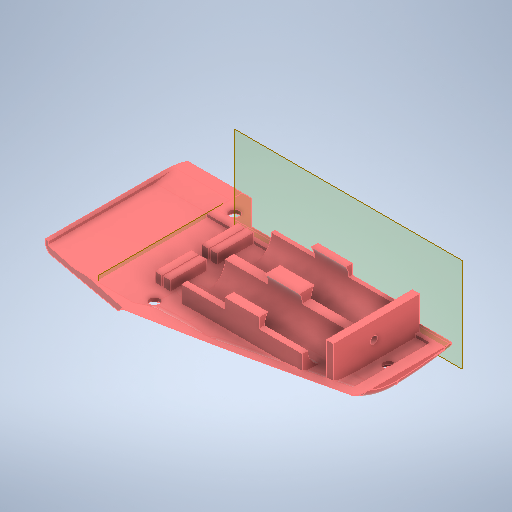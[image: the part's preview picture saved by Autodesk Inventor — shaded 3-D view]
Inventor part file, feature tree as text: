
AUTODESK INVENTOR PART (.ipt)
format: ipt  version: 2025 (Build 290162000, 162)  size: 3,606,528 bytes
history: native  units: in
note: dims shown in document units (in); Inventor stores cm internally (conversion verified against a paired STEP export)
features: extrude x48, sketch x39, fillet x33, other x28, reference x25, chamfer x10, projected_geometry x9, mirror x3, hole x1
ambient origin geometry x8: Origin, YZ Plane, XZ Plane, XY Plane, X Axis, Y Axis, Z Axis, Center Point
bodies: Body1 (feature_tree)
feature tree (196):
  other  "ソリッド1"
  sketch  "スケッチ1"
  extrude  "押し出し1"  Depth=3.3465in
  sketch  "スケッチ4"
  extrude  "押し出し4"  Depth=0.2756in
  extrude  "押し出し5"  Depth=9.8425in
  extrude  "押し出し6"  Depth=0.8661in TaperAngle=0.0deg
  extrude  "押し出し7"  Depth=0.8268in
  chamfer  "面取り1"  Distance=0.1181in
  chamfer  "面取り2"  Distance=0.1181in
  chamfer  "面取り3"  Distance=1.8504in
  chamfer  "面取り4"  Distance=1.1024in
  other  "作業平面3"
  other  "作業平面5"
  extrude  "押し出し8"  Depth=1.5354in
  other  "作業平面6"
  mirror  "ミラー1"
  chamfer  "面取り5"  Distance=3.3465in
  extrude  "押し出し9"  Depth=3.3465in TaperAngle=0.0deg
  fillet  "フィレット27"  Radius=3.3465in
  fillet  "フィレット28"  Radius=3.3465in
  fillet  "フィレット29"  Radius=0.1181in
  fillet  "フィレット30"  Radius=0.1181in
  fillet  "フィレット32"  Radius=0.1181in
  fillet  "フィレット35"  Radius=0.1181in
  fillet  "フィレット36"  Radius=0.3937in
  fillet  "フィレット37"  Radius=0.1575in
  fillet  "フィレット38"  Radius=0.7087in
  fillet  "フィレット42"  [1 undecoded]
  fillet  "フィレット43"  Radius=0.3543in
  fillet  "フィレット44"  Radius=1.9685in
  fillet  "フィレット45"  Radius=2.0866in
  other  "作業平面7"
  extrude  "押し出し10"  Depth=0.1969in
  fillet  "フィレット46"  Radius=0.1969in
  other  "作業平面8"
  extrude  "押し出し11"  Depth=0.7874in
  sketch  "スケッチ10"
  extrude  "押し出し12"  Depth=0.0787in
  extrude  "押し出し13"  Depth=0.3937in
  chamfer  "面取り6"  Distance=0.1181in
  sketch  "スケッチ11"
  chamfer  "面取り7"  Distance=0.1181in
  extrude  "押し出し14"  Depth=0.0354in
  chamfer  "面取り8"  Distance=0.0394in
  chamfer  "面取り9"  Distance=0.0787in
  extrude  "押し出し15"  Depth=0.0118in
  chamfer  "面取り10"  Distance=0.0354in
  other  "作業平面9"
  other  "作業平面10"
  extrude  "押し出し16"  [1 undecoded]
  fillet  "フィレット47"  Radius=0.0394in
  fillet  "フィレット48"  Radius=0.0394in
  fillet  "フィレット49"  Radius=0.0394in
  mirror  "ミラー7"
  mirror  "ミラー8"
  fillet  "フィレット58"  Radius=0.8268in
  fillet  "フィレット59"  Radius=0.0787in
  fillet  "フィレット60"  Radius=0.8268in
  fillet  "フィレット61"  Radius=1.1681in
  fillet  "フィレット62"  Radius=1.1681in
  fillet  "フィレット63"  Radius=0.6299in
  other  "作業平面11"
  extrude  "押し出し17"  TaperAngle=45.0deg  [1 undecoded]
  extrude  "押し出し18"  Depth=0.3937in
  extrude  "押し出し19"  Depth=1.1811in TaperAngle=0.0deg
  extrude  "押し出し20"  Depth=0.3543in TaperAngle=45.0deg
  other  "作業平面13"
  extrude  "押し出し21"  Depth=0.0787in
  fillet  "フィレット66"  Radius=0.1181in
  fillet  "フィレット67"  Radius=0.0709in
  extrude  "押し出し22"  Depth=0.0394in TaperAngle=45.0deg
  other  "作業平面14"
  extrude  "押し出し23"  Depth=0.0394in TaperAngle=45.0deg
  other  "作業平面15"
  extrude  "押し出し24"  Depth=0.0591in TaperAngle=0.0deg
  extrude  "押し出し25"  Depth=0.1969in TaperAngle=45.0deg
  other  "作業平面16"
  extrude  "押し出し26"  Depth=0.0591in TaperAngle=0.0deg
  extrude  "押し出し27"  Depth=3.937in
  other  "作業平面17"
  extrude  "押し出し28"  Depth=1.9685in
  extrude  "押し出し29"  Depth=0.1181in
  sketch  "スケッチ29"
  extrude  "押し出し30"  Depth=0.1181in
  extrude  "押し出し31"  Depth=0.0787in
  extrude  "押し出し32"  Depth=0.0197in
  extrude  "押し出し33"  Depth=0.0197in
  other  "作業平面18"
  extrude  "押し出し34"  Depth=0.3937in
  extrude  "押し出し35"  Depth=0.1181in
  fillet  "フィレット68"  [1 undecoded]
  fillet  "フィレット69"  Radius=1.1811in
  fillet  "フィレット70"  Radius=0.0787in
  fillet  "フィレット71"  Radius=0.1181in
  fillet  "フィレット72"  Radius=0.0197in
  extrude  "押し出し36"  Depth=0.0787in TaperAngle=0.0deg
  other  "作業平面19"
  fillet  "フィレット74"  Radius=0.9949in
  fillet  "フィレット75"  Radius=0.3937in
  fillet  "フィレット76"  Radius=0.0472in
  sketch  "スケッチ33"
  extrude  "押し出し39"  Depth=0.0669in
  extrude  "押し出し40"  Depth=0.0079in
  sketch  "スケッチ35"
  extrude  "押し出し41"  Depth=0.2756in
  other  "作業平面20"
  extrude  "押し出し42"  Depth=0.3543in
  sketch  "スケッチ37"
  extrude  "押し出し43"  Depth=0.3543in
  extrude  "押し出し44"  Depth=0.2756in
  sketch  "スケッチ38"
  hole  "穴2"  [1 undecoded]
  other  "作業平面21"
  sketch  "スケッチ40"
  extrude  "押し出し49"  Depth=0.0787in
  extrude  "押し出し50"  Depth=0.0079in
  extrude  "押し出し51"  Depth=0.1181in
  extrude  "押し出し52"  Depth=0.0787in
  extrude  "押し出し53"  Depth=0.0079in
  extrude  "押し出し54"  Depth=0.1181in
  other  "作業平面22"
  extrude  "押し出し55"  Depth=0.2756in TaperAngle=0.0deg
  extrude  "押し出し56"  Depth=0.1464in
  projected_geometry  "投影ループ2"
  sketch  "スケッチ5"
  projected_geometry  "投影ループ3"
  sketch  "スケッチ6"
  projected_geometry  "投影ループ4"
  other  "作業平面2"
  other  "作業平面4"
  sketch  "スケッチ7"
  sketch  "スケッチ8"
  projected_geometry  "投影ループ5"
  sketch  "スケッチ9"
  sketch  "スケッチ12"
  sketch  "スケッチ13"
  sketch  "スケッチ14"
  sketch  "スケッチ15"
  sketch  "スケッチ16"
  sketch  "スケッチ18"
  sketch  "スケッチ19"
  sketch  "スケッチ20"
  sketch  "スケッチ21"
  reference  "参照1"
  reference  "参照2"
  reference  "参照3"
  reference  "参照4"
  reference  "参照5"
  sketch  "スケッチ22"
  reference  "参照6"
  reference  "参照7"
  sketch  "スケッチ23"
  reference  "参照8"
  reference  "参照9"
  reference  "参照10"
  reference  "参照11"
  reference  "参照12"
  reference  "参照13"
  sketch  "スケッチ24"
  projected_geometry  "投影ループ6"
  sketch  "スケッチ25"
  sketch  "スケッチ26"
  sketch  "スケッチ27"
  sketch  "スケッチ28"
  reference  "参照14"
  reference  "参照15"
  other  "スケッチ円形状パターン1"
  sketch  "スケッチ30"
  reference  "参照16"
  sketch  "スケッチ31"
  reference  "参照17"
  reference  "参照18"
  reference  "参照19"
  reference  "参照21"
  reference  "参照22"
  reference  "参照23"
  reference  "参照24"
  reference  "参照25"
  reference  "参照29"
  sketch  "スケッチ32"
  sketch  "スケッチ34"
  sketch  "スケッチ36"
  projected_geometry  "投影ループ7"
  sketch  "スケッチ41"
  sketch  "スケッチ42"
  projected_geometry  "投影ループ8"
  projected_geometry  "投影ループ9"
  sketch  "スケッチ43"
  projected_geometry  "投影ループ10"
  other  "<userpath>\OneDrive\ドキュメント\New Controller\Hardware\Assembly.iam"
  other  "Assembly.iam"
  other  "Nano33BLE:1"
  other  "Cuicuit:1"
  other  "switch:1"
  other  "mini vibrator:1"
note: 5 required parameter values undecoded (feature->parameter linkage not recoverable at this tier; creation-order binding heuristic only, values carry confidence <= 0.55)
